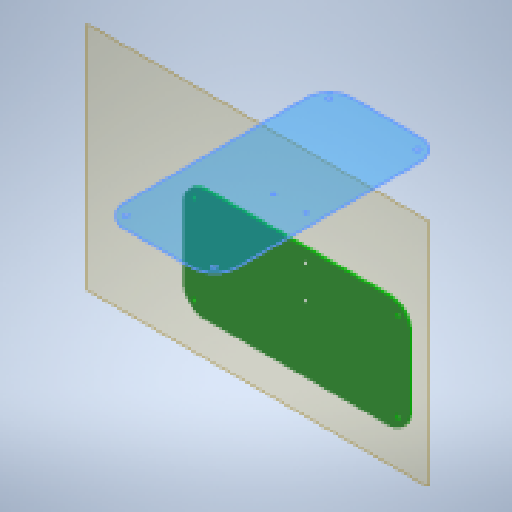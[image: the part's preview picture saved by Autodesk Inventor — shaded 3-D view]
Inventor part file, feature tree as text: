
AUTODESK INVENTOR PART (.ipt)
format: ipt  version: 2024.2 (Build 282272000, 272)  size: 157,696 bytes
history: native  units: mm
features: other x7, extrude x2, sketch x2, reference x2
ambient origin geometry x8: Origin, YZ Plane, XZ Plane, XY Plane, X Axis, Y Axis, Z Axis, Center Point
bodies: Body1 (feature_tree)
feature tree (13):
  other  "Твердое тело1"
  other  "РабПлоскость1"
  extrude  "Выдавливание1"  Depth=15.0mm
  sketch  "Эскиз2"
  other  "РабПлоскость2"
  extrude  "Выдавливание2"  Depth=76.0mm
  sketch  "Эскиз1"
  reference  "Ссылка1"
  reference  "Ссылка2"
  other  "<userpath>\Documents\Artist-v2\3D\Робот.iam"
  other  "Робот.iam"
  other  "DM-OLED096-636--3DModel-STEP-56544:1"
  other  "крышка:1"
